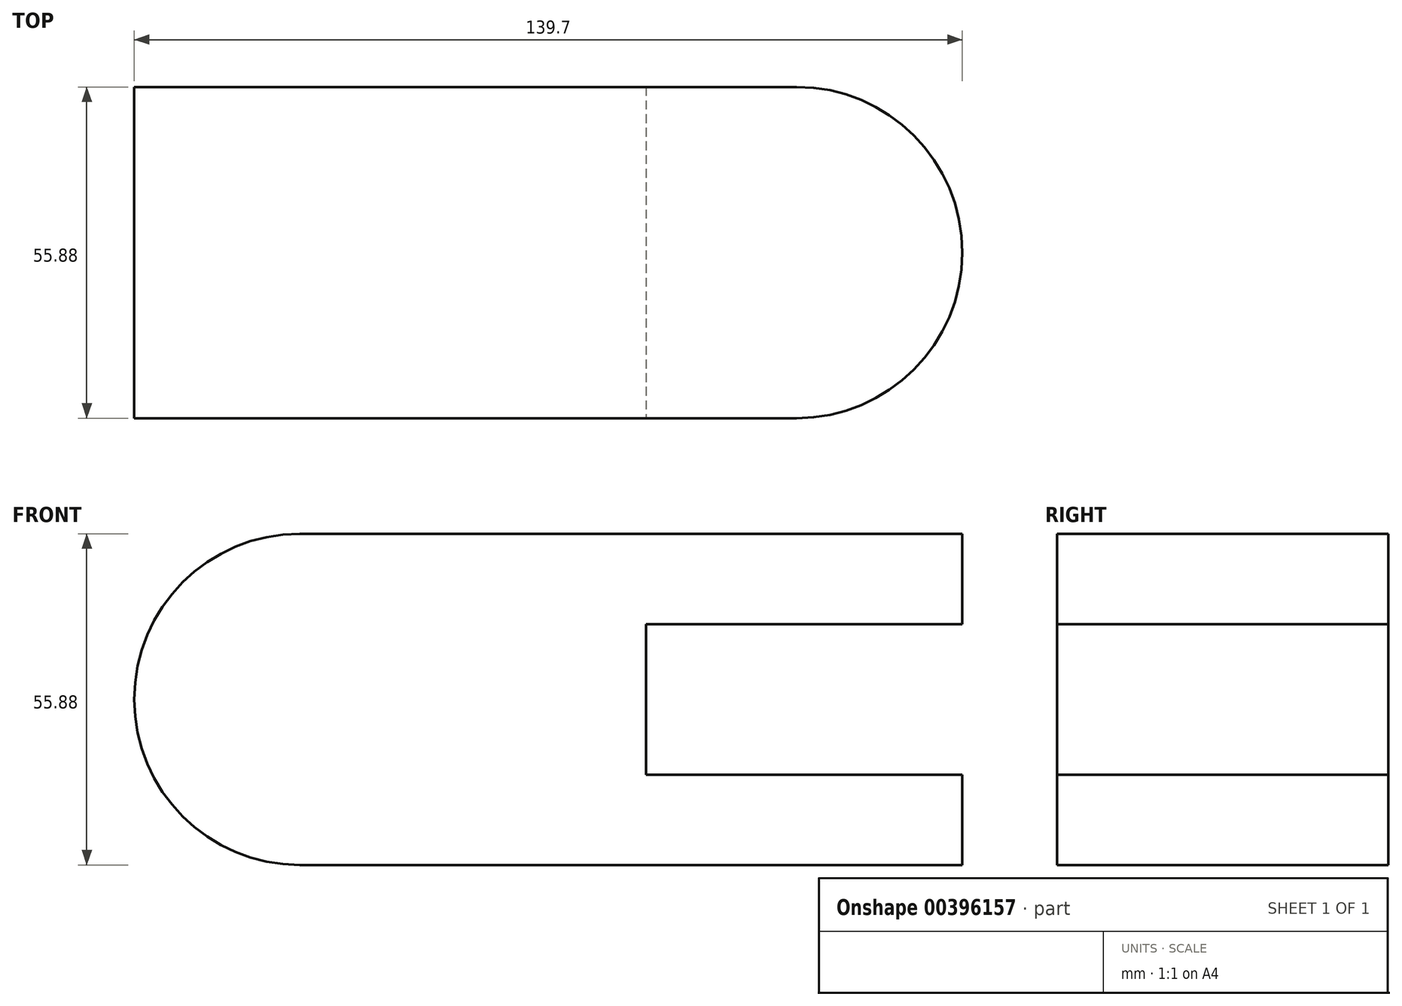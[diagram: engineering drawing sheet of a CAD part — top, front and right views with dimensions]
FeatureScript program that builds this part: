
annotation { "Feature Type Name" : "Feature", "Feature Type Description" : "" }
export const myFeature = defineFeature(function(context is Context, id is Id, definition is map)
    precondition{}
    {
        {
            var Q0;
            Q0=qCreatedBy(makeId("Top.planeOp"),FACE);
            var sketch = newSketch(context, id + "F0", { "sketchPlane" : qUnion([Q0])});
            skLineSegment(sketch, "E0.bottom", {"start": v(-50.3, 6.97) * mm, "end": v(89.4, 6.97) * mm});
            skLineSegment(sketch, "E0.top", {"start": v(-50.3, -48.91) * mm, "end": v(89.4, -48.91) * mm});
            skLineSegment(sketch, "E0.left", {"start": v(-50.3, 6.97) * mm, "end": v(-50.3, -48.91) * mm});
            skLineSegment(sketch, "E0.right", {"start": v(89.4, 6.97) * mm, "end": v(89.4, -48.91) * mm});
            skSolve(sketch);
        }
        {
            var Q0;
            Q0 = qSketchRegion(id + "F0", true);
            extrude(context, id + "F1", {"entities" : qUnion([Q0]), "depth" : 55.88 * mm});
        }
        {
            var Q0;
            Q0=makeQuery(id+"F1.opExtrude","CAP_EDGE",EDGE,{"disambiguationData":[OSD([sQuery(id+"F0.wireOp",EDGE,"E0.left")])],"isStart":true});
            var Q1;
            Q1=makeQuery(id+"F1.opExtrude","CAP_EDGE",EDGE,{"disambiguationData":[OSD([sQuery(id+"F0.wireOp",EDGE,"E0.left")])],"isStart":false});
            var Q2;
            Q2=makeQuery(id+"F1.opExtrude","SWEPT_EDGE",EDGE,{"disambiguationData":[OSD([sQuery(id+"F0.wireOp",EDGE,"E0.top"),sQuery(id+"F0.wireOp",EDGE,"E0.right")])]});
            var Q3;
            Q3=makeQuery(id+"F1.opExtrude","SWEPT_EDGE",EDGE,{"disambiguationData":[OSD([sQuery(id+"F0.wireOp",EDGE,"E0.bottom"),sQuery(id+"F0.wireOp",EDGE,"E0.right")])]});
            fillet(context, id + "F2", {"entities" : qUnion([Q0, Q1, Q2, Q3]), "radius" : 27.94 * mm, "tangentPropagation" : true, "allowEdgeOverflow" : false});
        }
        {
            var Q0;
            Q0=qCreatedBy(makeId("Front.planeOp"),FACE);
            var sketch = newSketch(context, id + "F3", { "sketchPlane" : qUnion([Q0])});
            skLineSegment(sketch, "E1.bottom", {"start": v(36.06, 40.64) * mm, "end": v(89.4, 40.64) * mm});
            skLineSegment(sketch, "E1.top", {"start": v(36.06, 15.24) * mm, "end": v(89.4, 15.24) * mm});
            skLineSegment(sketch, "E1.left", {"start": v(36.06, 40.64) * mm, "end": v(36.06, 15.24) * mm});
            skLineSegment(sketch, "E1.right", {"start": v(89.4, 40.64) * mm, "end": v(89.4, 15.24) * mm});
            skSolve(sketch);
        }
        {
            var Q0;
            Q0 = qSketchRegion(id + "F3", true);
            extrude(context, id + "F4", {"entities" : qUnion([Q0]), "operationType" : NewBodyOperationType.REMOVE, "endBound" : BoundingType.THROUGH_ALL, "oppositeDirection" : true, "depth" : 25.4 * mm, "hasSecondDirection" : true, "secondDirectionBound" : SecondDirectionBoundingType.THROUGH_ALL, "secondDirectionOppositeDirection" : false, "secondDirectionDepth" : 25.4 * mm});
        }
    });
